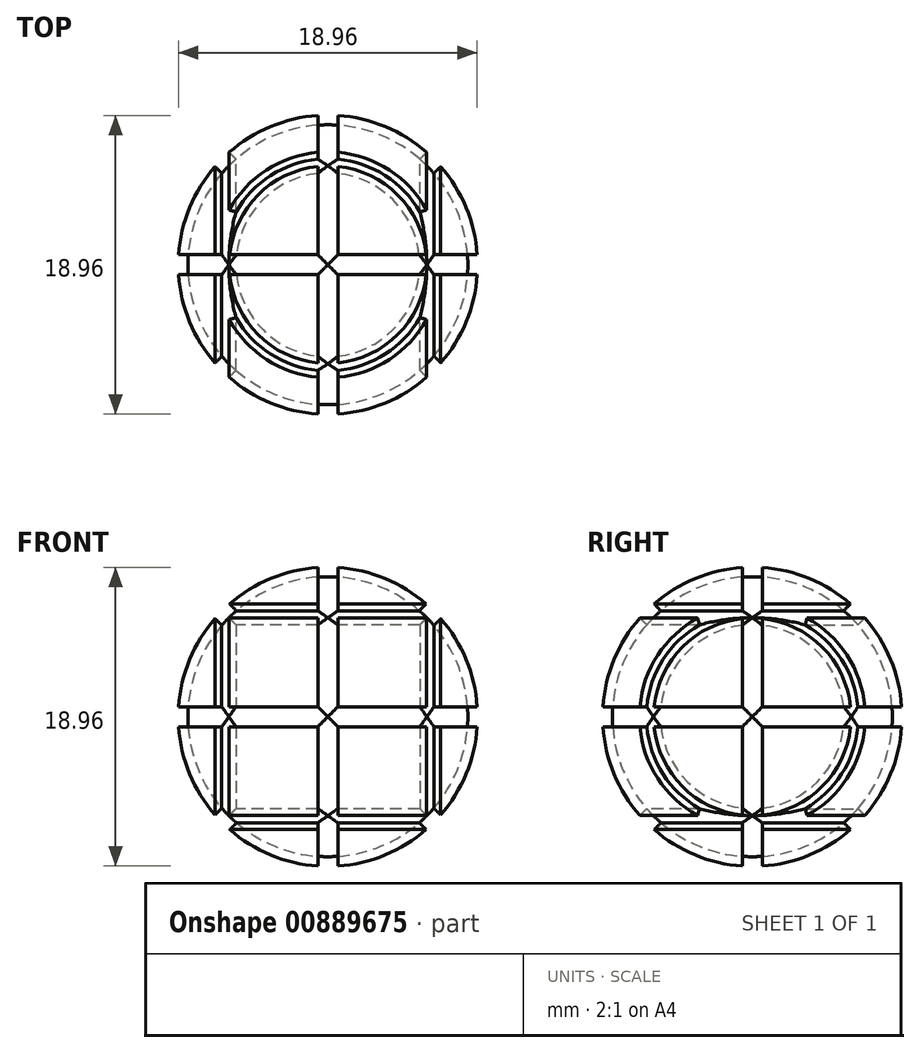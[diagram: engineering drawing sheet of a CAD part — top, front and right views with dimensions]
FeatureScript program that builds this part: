
annotation { "Feature Type Name" : "Feature", "Feature Type Description" : "" }
export const myFeature = defineFeature(function(context is Context, id is Id, definition is map)
    precondition{}
    {
        {
            var Q0;
            Q0=qCreatedBy(makeId("Front.planeOp"),FACE);
            var sketch = newSketch(context, id + "F0", { "sketchPlane" : qUnion([Q0])});
            skArc(sketch, "E0", {"start": v(0, -9.53) * mm, "mid": v(9.53, 0) * mm, "end": v(0, 9.53) * mm});
            skLineSegment(sketch, "E1", {"start": v(0, 9.53) * mm, "end": v(0, -9.53) * mm});
            skSolve(sketch);
        }
        {
            var Q0;
            Q0=makeQuery(id+"F0.imprint","IMPRINT",FACE,{"disambiguationData":[TD([[makeQuery(id+"F0.imprint","IMPRINT",EDGE,{"derivedFrom":sQuery(id+"F0.wireOp",EDGE,"E0")}),1.0]])]});
            var Q1;
            Q1=sQuery(id+"F0.wireOp",EDGE,"E1");
            revolve(context, id + "F1", {"surfaceOperationType" : NewSurfaceOperationType.NEW, "entities" : qUnion([Q0]), "axis" : qUnion([Q1]), "revolveType" : RevolveType.FULL});
        }
        {
            var Q0;
            Q0=qCreatedBy(makeId("Front.planeOp"),FACE);
            var sketch = newSketch(context, id + "F2", { "sketchPlane" : qUnion([Q0])});
            skLineSegment(sketch, "E2.bottom", {"start": v(8.9, 0.64) * mm, "end": v(10.16, 0.64) * mm});
            skLineSegment(sketch, "E2.top", {"start": v(8.9, -0.63) * mm, "end": v(10.16, -0.63) * mm});
            skLineSegment(sketch, "E2.left", {"start": v(8.9, 0.64) * mm, "end": v(8.9, -0.64) * mm});
            skLineSegment(sketch, "E2.right", {"start": v(10.16, 0.64) * mm, "end": v(10.16, -0.64) * mm});
            skLineSegment(sketch, "E3", {"start": v(8.9, 0) * mm, "end": v(0, 0) * mm, "construction": true});
            skLineSegment(sketch, "E4", {"start": v(0, 0) * mm, "end": v(0, 4.36) * mm, "construction": true});
            skLineSegment(sketch, "E5", {"start": v(0, 0) * mm, "end": v(6.29, 6.29) * mm, "construction": true});
            skLineSegment(sketch, "E6", {"start": v(5.84, 6.74) * mm, "end": v(6.29, 6.29) * mm});
            skLineSegment(sketch, "E7", {"start": v(6.29, 6.29) * mm, "end": v(6.74, 5.84) * mm});
            skLineSegment(sketch, "E8", {"start": v(6.74, 5.84) * mm, "end": v(7.63, 6.74) * mm});
            skLineSegment(sketch, "E9", {"start": v(7.63, 6.74) * mm, "end": v(6.74, 7.63) * mm});
            skLineSegment(sketch, "E10", {"start": v(6.74, 7.63) * mm, "end": v(5.84, 6.74) * mm});
            skLineSegment(sketch, "E11.MirrorCS", {"start": v(5.84, -6.74) * mm, "end": v(6.29, -6.29) * mm});
            skLineSegment(sketch, "E12.MirrorCS", {"start": v(6.29, -6.29) * mm, "end": v(6.74, -5.84) * mm});
            skLineSegment(sketch, "E13.MirrorCS", {"start": v(6.74, -7.63) * mm, "end": v(5.84, -6.74) * mm});
            skLineSegment(sketch, "E14.MirrorCS", {"start": v(6.74, -5.84) * mm, "end": v(7.63, -6.74) * mm});
            skLineSegment(sketch, "E15.MirrorCS", {"start": v(7.63, -6.74) * mm, "end": v(6.74, -7.63) * mm});
            skSolve(sketch);
        }
        {
            var Q0;
            Q0 = qSketchRegion(id + "F2", true);
            var Q1;
            Q1=sQuery(id+"F2.wireOp",EDGE,"E4");
            revolve(context, id + "F3", {"operationType" : NewBodyOperationType.REMOVE, "surfaceOperationType" : NewSurfaceOperationType.NEW, "entities" : qUnion([Q0]), "axis" : qUnion([Q1]), "revolveType" : RevolveType.FULL, "oppositeDirection" : true});
        }
        {
            var Q0;
            Q0=qCreatedBy(makeId("Front.planeOp"),FACE);
            var sketch = newSketch(context, id + "F4", { "sketchPlane" : qUnion([Q0])});
            skLineSegment(sketch, "E16.bottom", {"start": v(-0.64, 10.16) * mm, "end": v(0.64, 10.16) * mm});
            skLineSegment(sketch, "E16.top", {"start": v(-0.64, 8.9) * mm, "end": v(0.64, 8.9) * mm});
            skLineSegment(sketch, "E16.left", {"start": v(-0.64, 10.16) * mm, "end": v(-0.64, 8.9) * mm});
            skLineSegment(sketch, "E16.right", {"start": v(0.64, 10.16) * mm, "end": v(0.64, 8.9) * mm});
            skLineSegment(sketch, "E17", {"start": v(0, 0) * mm, "end": v(0, 8.9) * mm, "construction": true});
            skLineSegment(sketch, "E18", {"start": v(0, 0) * mm, "end": v(-3.51, 0) * mm, "construction": true});
            skLineSegment(sketch, "E19", {"start": v(0, 0) * mm, "end": v(-6.29, 6.29) * mm, "construction": true});
            skLineSegment(sketch, "E20", {"start": v(-6.29, 6.29) * mm, "end": v(-5.84, 6.74) * mm});
            skLineSegment(sketch, "E21", {"start": v(-5.84, 6.74) * mm, "end": v(-6.74, 7.63) * mm});
            skLineSegment(sketch, "E22", {"start": v(-6.74, 7.63) * mm, "end": v(-7.63, 6.74) * mm});
            skLineSegment(sketch, "E23", {"start": v(-7.63, 6.74) * mm, "end": v(-6.74, 5.84) * mm});
            skLineSegment(sketch, "E24", {"start": v(-6.74, 5.84) * mm, "end": v(-6.29, 6.29) * mm});
            skLineSegment(sketch, "E25.MirrorCS", {"start": v(6.74, 7.63) * mm, "end": v(7.63, 6.74) * mm});
            skLineSegment(sketch, "E26.MirrorCS", {"start": v(7.63, 6.74) * mm, "end": v(6.74, 5.84) * mm});
            skLineSegment(sketch, "E27.MirrorCS", {"start": v(6.29, 6.29) * mm, "end": v(5.84, 6.74) * mm});
            skLineSegment(sketch, "E28.MirrorCS", {"start": v(6.74, 5.84) * mm, "end": v(6.29, 6.29) * mm});
            skLineSegment(sketch, "E29.MirrorCS", {"start": v(5.84, 6.74) * mm, "end": v(6.74, 7.63) * mm});
            skSolve(sketch);
        }
        {
            var Q0;
            Q0 = qSketchRegion(id + "F4", true);
            var Q1;
            Q1=sQuery(id+"F4.wireOp",EDGE,"E18");
            revolve(context, id + "F5", {"operationType" : NewBodyOperationType.REMOVE, "surfaceOperationType" : NewSurfaceOperationType.NEW, "entities" : qUnion([Q0]), "axis" : qUnion([Q1]), "revolveType" : RevolveType.FULL, "oppositeDirection" : true});
        }
        {
            var Q0;
            Q0=qCreatedBy(makeId("Top.planeOp"),FACE);
            var sketch = newSketch(context, id + "F6", { "sketchPlane" : qUnion([Q0])});
            skLineSegment(sketch, "E30.bottom", {"start": v(8.9, -0.64) * mm, "end": v(10.16, -0.64) * mm});
            skLineSegment(sketch, "E30.top", {"start": v(8.9, 0.64) * mm, "end": v(10.16, 0.64) * mm});
            skLineSegment(sketch, "E30.left", {"start": v(8.9, -0.63) * mm, "end": v(8.9, 0.63) * mm});
            skLineSegment(sketch, "E30.right", {"start": v(10.16, -0.64) * mm, "end": v(10.16, 0.64) * mm});
            skLineSegment(sketch, "E31", {"start": v(0, 0) * mm, "end": v(8.9, 0) * mm, "construction": true});
            skLineSegment(sketch, "E32", {"start": v(0, 0) * mm, "end": v(0, 2.22) * mm, "construction": true});
            skSolve(sketch);
        }
        {
            var Q0;
            Q0 = qSketchRegion(id + "F6", true);
            var Q1;
            Q1=sQuery(id+"F6.wireOp",EDGE,"E32");
            revolve(context, id + "F7", {"operationType" : NewBodyOperationType.REMOVE, "surfaceOperationType" : NewSurfaceOperationType.NEW, "entities" : qUnion([Q0]), "axis" : qUnion([Q1]), "revolveType" : RevolveType.FULL, "oppositeDirection" : true});
        }
    });
